# Revit family: Door_Access_Fire-Floor_Acudor_FRFD
name_source: partatom
category: Generic Models
units: mm (PartAtom-declared; Revit-internal decimal feet)

## family parameters
Can host rebar = No
Cut with Voids When Loaded = No
Host = Face
Maintain Annotation Orientation = No
Part Type = Normal
Room Calculation Point = No
Round Connector Dimension = Use Diameter
Shared = No

## types (9) — shared parameters
Capacity = Live Load 150 lbs/sqft
Default Elevation = 0' - 0"
Description = Acudor Fire Rated Flush Floor Access Door - FRFD as Specified
Fire Performance = 2 HR Floor Ceiling Assembly
Green Building-LEED = http://www.arcat.com
Manufacturer = Acudor Products Inc
Manufacturer Fax = 973-575-5160
Manufacturer Website = http://www.acudor.com
Model = FRFD
Product Data = http://www.arcat.com
Revision = R1_2017-03
Sales Information = http://www.acudor.com
Standards Conformance = NFPA 288  ;   ASTM E119  ;  Warnock Hersey International
URL = http://www.acudor.com
Unit Depth = 0' - 8"
zero-valued in all types: Expected Lifespan (Years), Maintenance Schedule (Months), Warranty Duration (Years)

## per-type parameters (varying)
| type | Clear Opening Height | Clear Opening Width | Door Height | Door Width | Opening Height | Opening Width | Overall Height | Overall Width | Unit Height | Unit Weight | Unit Width |
| 48 x 48 Nom | 3' - 8" | 4' - 0" | 4' - 9 1/2" | 4' - 9 1/2" | 4' - 0" | 4' - 0" | 4' - 10" | 4' - 10" | 4' - 0" | 280 | 4' - 0" |
| 42 x 42 Nom | 3' - 2" | 3' - 6" | 4' - 3 1/2" | 4' - 3 1/2" | 3' - 6" | 3' - 6" | 4' - 4" | 4' - 4" | 3' - 6" | 250 | 3' - 6" |
| 36 x 48 Nom | 2' - 8" | 4' - 0" | 4' - 9 1/2" | 3' - 9 1/2" | 4' - 0" | 3' - 0" | 4' - 10" | 3' - 10" | 4' - 0" | 240 | 3' - 0" |
| 36 x 36 Nom | 2' - 8" | 3' - 0" | 3' - 9 1/2" | 3' - 9 1/2" | 3' - 0" | 3' - 0" | 3' - 10" | 3' - 10" | 3' - 0" | 190 | 3' - 0" |
| 30 x 36 Nom | 2' - 2" | 3' - 0" | 3' - 9 1/2" | 3' - 3 1/2" | 3' - 0" | 2' - 6" | 3' - 10" | 3' - 4" | 3' - 0" | 160 | 2' - 6" |
| 30 x 30 Nom | 2' - 2" | 2' - 6" | 3' - 3 1/2" | 3' - 3 1/2" | 2' - 6" | 2' - 6" | 3' - 4" | 3' - 4" | 2' - 6" | 130 | 2' - 6" |
| 24 x 48 Nom | 1' - 8" | 4' - 0" | 4' - 9 1/2" | 2' - 9 1/2" | 4' - 0" | 2' - 0" | 4' - 10" | 2' - 10" | 4' - 0" | 160 | 2' - 0" |
| 24 x 36 Nom | 1' - 8" | 3' - 0" | 3' - 9 1/2" | 2' - 9 1/2" | 3' - 0" | 2' - 0" | 3' - 10" | 2' - 10" | 3' - 0" | 140 | 2' - 0" |
| 24 x 24 Nom | 1' - 8" | 2' - 0" | 2' - 9 1/2" | 2' - 9 1/2" | 2' - 0" | 2' - 0" | 2' - 10" | 2' - 10" | 2' - 0" | 80 | 2' - 0" |

## geometry (parser evidence)
native form markers: Sweep x2
no freeform markers — native parametric forms only
